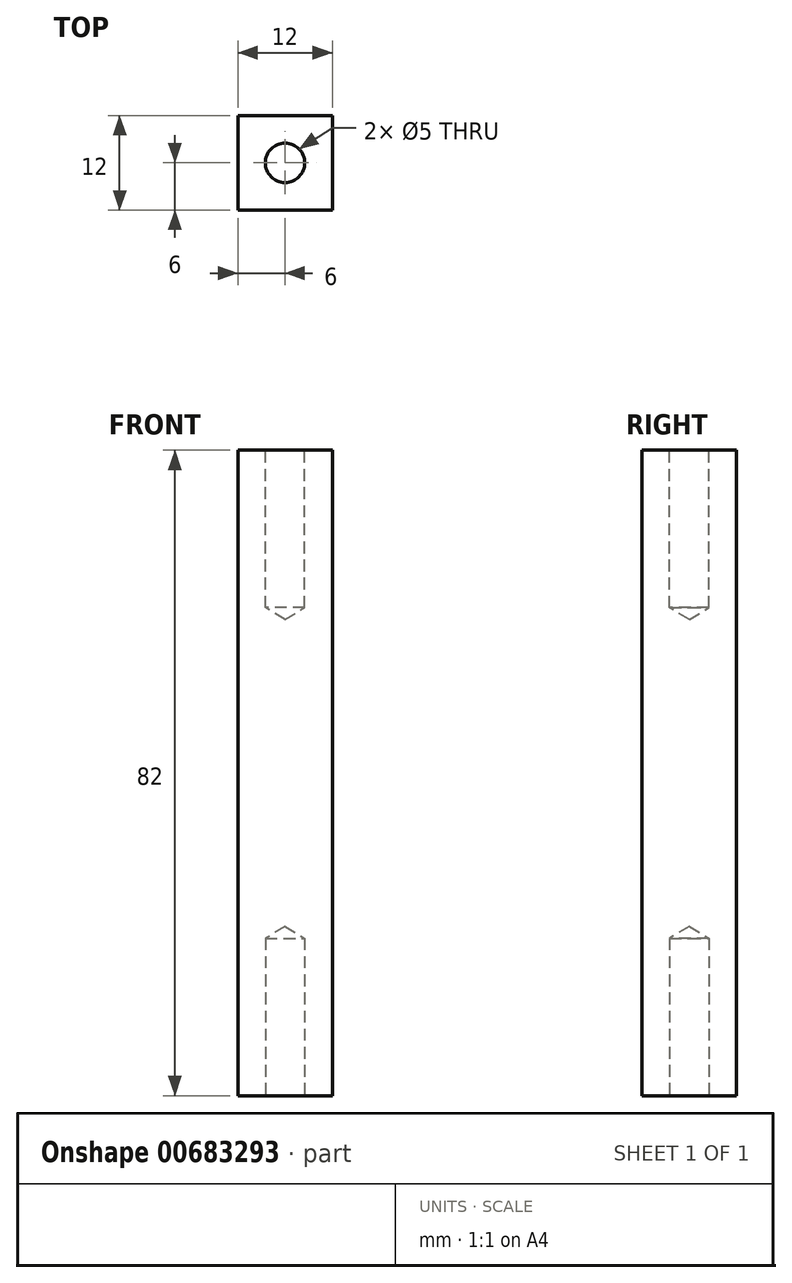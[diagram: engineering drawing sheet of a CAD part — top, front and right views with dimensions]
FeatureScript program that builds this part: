
annotation { "Feature Type Name" : "Feature", "Feature Type Description" : "" }
export const myFeature = defineFeature(function(context is Context, id is Id, definition is map)
    precondition{}
    {
        {
            var Q0;
            Q0=qCreatedBy(makeId("Top.planeOp"),FACE);
            var sketch = newSketch(context, id + "F0", { "sketchPlane" : qUnion([Q0])});
            skLineSegment(sketch, "E0.bottom", {"start": v(6, 6) * mm, "end": v(-6, 6) * mm});
            skLineSegment(sketch, "E0.top", {"start": v(6, -6) * mm, "end": v(-6, -6) * mm});
            skLineSegment(sketch, "E0.left", {"start": v(6, 6) * mm, "end": v(6, -6) * mm});
            skLineSegment(sketch, "E0.right", {"start": v(-6, 6) * mm, "end": v(-6, -6) * mm});
            skPoint(sketch, "E0.middle", {"position": v(0, 0) * mm});
            skSolve(sketch);
        }
        {
            var Q0;
            Q0=makeQuery(id+"F0.imprint","IMPRINT",FACE,{"disambiguationData":[TD([[makeQuery(id+"F0.imprint","IMPRINT",EDGE,{"derivedFrom":sQuery(id+"F0.wireOp",EDGE,"E0.bottom")}),1.0]])]});
            extrude(context, id + "F1", {"entities" : qUnion([Q0]), "oppositeDirection" : true, "depth" : 82 * mm, "offsetDistance" : 25 * mm});
        }
        {
            var Q0;
            Q0=makeQuery(id+"F1.opExtrude","CAP_FACE",FACE,{"disambiguationData":[OSD([sQuery(id+"F0.wireOp",EDGE,"E0.bottom"),sQuery(id+"F0.wireOp",EDGE,"E0.top"),sQuery(id+"F0.wireOp",EDGE,"E0.left"),sQuery(id+"F0.wireOp",EDGE,"E0.right")])],"isStart":true});
            var sketch = newSketch(context, id + "F2", { "sketchPlane" : qUnion([Q0])});
            skCircle(sketch, "E1", {"center": v(0, 0) * mm, "radius": 3 * mm, "construction": true});
            skSolve(sketch);
        }
        {
            var Q0;
            Q0=sQuery(id+"F2.wireOp",VERTEX,"E1.center");
            var Q1;
            Q1=makeQuery(id+"F1.opExtrude","SWEPT_BODY",BODY,{"disambiguationData":[OSD([sQuery(id+"F0.wireOp",EDGE,"E0.bottom"),sQuery(id+"F0.wireOp",EDGE,"E0.top"),sQuery(id+"F0.wireOp",EDGE,"E0.left"),sQuery(id+"F0.wireOp",EDGE,"E0.right")])]});
            hole(context, id + "F3", {"style" : HoleStyle.SIMPLE, "endStyle" : HoleEndStyle.BLIND, "standardTappedOrClearance" : lookupTablePath({ "standard" : "ISO", "engagement" : "75%", "pitch" : "1 mm", "size" : "M6", "type" : "Tapped" }), "standardBlindInLast" : lookupTablePath({ "standard" : "ISO", "engagement" : "75%", "pitch" : "1 mm", "size" : "M6", "type" : "Tapped" }), "holeDiameter" : 5 * mm, "majorDiameter" : 6 * mm, "showTappedDepth" : true, "holeDepth" : 20 * mm, "isTappedThrough" : true, "tappedDepth" : 20 * mm, "tapClearance" : 0, "startFromSketch" : true, "locations" : qUnion([Q0]), "scope" : qUnion([Q1])});
        }
        {
            var Q0;
            Q0=makeQuery(id+"F1.opExtrude","CAP_FACE",FACE,{"disambiguationData":[OSD([sQuery(id+"F0.wireOp",EDGE,"E0.bottom"),sQuery(id+"F0.wireOp",EDGE,"E0.top"),sQuery(id+"F0.wireOp",EDGE,"E0.left"),sQuery(id+"F0.wireOp",EDGE,"E0.right")])],"isStart":false});
            var sketch = newSketch(context, id + "F4", { "sketchPlane" : qUnion([Q0])});
            skCircle(sketch, "E2", {"center": v(0, 0) * mm, "radius": 3 * mm, "construction": true});
            skSolve(sketch);
        }
        {
            var Q0;
            Q0=sQuery(id+"F4.wireOp",VERTEX,"E2.center");
            var Q1;
            Q1=makeQuery(id+"F1.opExtrude","SWEPT_BODY",BODY,{"disambiguationData":[OSD([sQuery(id+"F0.wireOp",EDGE,"E0.bottom"),sQuery(id+"F0.wireOp",EDGE,"E0.top"),sQuery(id+"F0.wireOp",EDGE,"E0.left"),sQuery(id+"F0.wireOp",EDGE,"E0.right")])]});
            hole(context, id + "F5", {"style" : HoleStyle.SIMPLE, "endStyle" : HoleEndStyle.BLIND, "standardTappedOrClearance" : lookupTablePath({ "standard" : "ISO", "engagement" : "75%", "pitch" : "1 mm", "size" : "M6", "type" : "Tapped" }), "standardBlindInLast" : lookupTablePath({ "standard" : "ISO", "engagement" : "75%", "pitch" : "1 mm", "size" : "M6", "type" : "Tapped" }), "holeDiameter" : 5 * mm, "majorDiameter" : 6 * mm, "showTappedDepth" : true, "holeDepth" : 20 * mm, "isTappedThrough" : true, "tappedDepth" : 20 * mm, "tapClearance" : 0, "startFromSketch" : true, "locations" : qUnion([Q0]), "scope" : qUnion([Q1])});
        }
    });
